# Revit family: L-PLT_곰솔
name_source: partatom
category: 수목
units: mm (PartAtom-declared; Revit-internal decimal feet)

## family parameters
OmniClass 번호 = 23.40.05.00
OmniClass 제목 = Plants and Planting Products
공유 = 아니오
렌더 모양 소스 = 패밀리 형상
로드될 때 보이드를 사용하여 절단 = 아니오
작업 기준면 기반 = 아니오
항상 수직 = 예

## types (7) — shared parameters
KBIMS_보급정보-저작자 = 림인포테크_MMJ
LIM_INFO_PL_구분 = 상록교목
LIM_INFO_PL_수목단위 = 주
LIM_INFO_PL_품명 = 곰솔
LIM_INFO_PL_학명 = Pinus thunbergii Parl.
LIM_INFO_버전 = 2022_V01
LIM_INFO_제작일 = 20211210
LIM_INFO_주의사항 = 재배포, 재가공, 판매 금지
R = 200  [stored 0.656168 ft]
건설정보분류체계-부위분류 = E985
뿌리분 높이 = 545
뿌리분 직경 = 1090
조달청표준공사코드-세부공종 = 10161599202810
콘 높이 = 273
zero-valued in all types: LIM_INFO_PL_M2당수량, LIM_INFO_PL_가격, LIM_INFO_PL_주당인정수량

## per-type parameters (varying)
| type | H | LIM_INFO_PL_규격 | 높이 |
| 곰솔 5.0H X 2.5W X 20R | 5000  [stored 16.4042 ft] | 5.0H X 2.5W X 20R | 5000  [stored 16.4042 ft] |
| 곰솔 4.0H X 2.0W X 15R | 4000 | 4.0H X 2.0W X 15R | 4000 |
| 곰솔 3.5H X 1.5W X 12R | 3500 | 3.5H X 1.5W X 12R | 3500 |
| 곰솔 3.0H X 1.2W X 10R | 3000 | 3.0H X 1.2W X 10R | 3000 |
| 곰솔 3.0H X 1.0W X 6R | 3000 | 3.0H X 1.0W X 6R | 3000 |
| 곰솔 2.5H X 0.8W | 2500  [stored 8.2021 ft] | 2.5H X 0.8W | 2500  [stored 8.2021 ft] |
| 곰솔 2.0H X 0.6W | 2000 | 2.0H X 0.6W | 2000 |

note: [stored X ft] marks values corroborated as IEEE doubles in the binary element streams (Revit-internal decimal feet)
